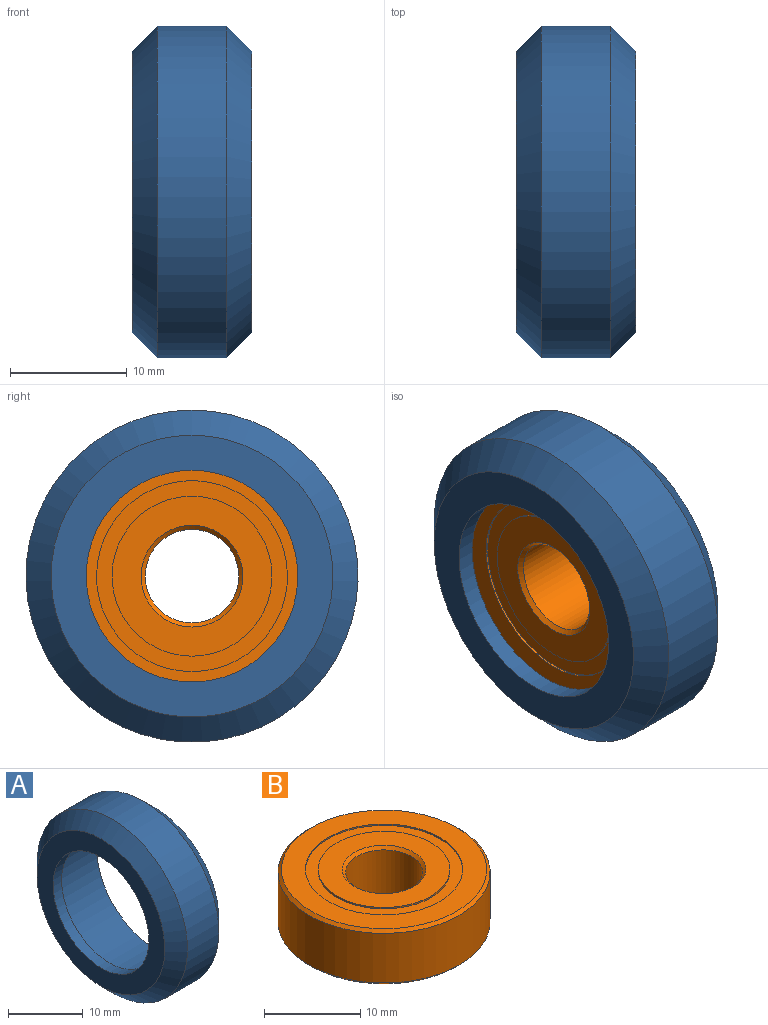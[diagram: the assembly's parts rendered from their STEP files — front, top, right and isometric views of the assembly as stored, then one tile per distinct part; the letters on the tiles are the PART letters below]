
ASSEMBLY  parts=2 mates=1
PART A: 8 faces, bbox 10.2x28.4x28.4 mm
  f0: cone r=14.2mm half-angle=45deg, axis (1,0,0), area 250.7mm2, adj f1,f7
  f1: plane 24.1x24.1mm, normal (-1,0,0), area 198.9mm2, adj f0,f2
  f2: cylinder r=9.05mm len=18.1mm, axis (-1,0,0), area 91mm2, adj f1,f3
  f3: plane 22.1x22.1mm, normal (1,0,0), area 126.3mm2, adj f2,f4
  f4: cylinder r=11.05mm len=22.1mm, axis (-1,0,0), area 597.1mm2, adj f3,f5
  f5: plane 24.1x24.1mm, normal (1,0,0), area 72.6mm2, adj f4,f6
  f6: cone r=12.05mm half-angle=45deg, axis (-1,0,0), area 250.7mm2, adj f5,f7
  f7: cylinder r=14.2mm len=28.4mm, axis (-1,0,0), area 526.4mm2, adj f0,f6
PART B: 156 faces, bbox 22x22x7 mm
  f0: cylinder r=8.16mm len=16.32mm, axis (0,0,1), area 9mm2, adj f6,f15
  f1: cylinder r=6.84mm len=13.68mm, axis (0,0,1), area 7.5mm2, adj f13,f15
  f2: cylinder r=8.16mm len=16.32mm, axis (0,0,1), area 9mm2, adj f7,f14
  f3: cone r=10.65mm half-angle=45deg, axis (0,0,1), area 33.7mm2, adj f4,f6
  f4: cylinder r=11mm len=22mm, axis (0,0,1), area 435.4mm2, adj f3,f5
  f5: cone r=11mm half-angle=45deg, axis (0,0,-1), area 33.7mm2, adj f4,f7
  f6: plane 21.3x21.3mm, normal (0,0,-1), area 147.2mm2, adj f0,f3
  f7: plane 21.3x21.3mm, normal (0,0,1), area 147.2mm2, adj f2,f5
  f8: cone r=4.35mm half-angle=45deg, axis (0,0,1), area 13mm2, adj f9,f12
  f9: cylinder r=4mm len=8mm, axis (0,0,1), area 158.3mm2, adj f8,f10
  f10: cone r=4mm half-angle=45deg, axis (0,0,-1), area 13mm2, adj f9,f13
  f11: cylinder r=6.84mm len=13.68mm, axis (0,0,1), area 7.5mm2, adj f12,f14
  f12: plane 13.68x13.68mm, normal (0,0,1), area 87.6mm2, adj f8,f11
  f13: plane 13.68x13.68mm, normal (0,0,-1), area 87.6mm2, adj f1,f10
  f14: plane 16.32x16.32mm, normal (0,0,1), area 62.1mm2, adj f2,f11
  f15: plane 16.32x16.32mm, normal (0,0,-1), area 62.1mm2, adj f0,f1
  f16: plane 1.59x1.53mm, normal (0,0,1), area 0.9mm2, adj f22,f23,f24,f25
  f17: torus R=7.5mm, axis (0,0,1), area 3.6mm2, adj f18,f22,f23,f25
  f18: cylinder r=8.16mm len=0.86mm, axis (0,0,1), area 0.1mm2, adj f17,f19,f22,f23
  f19: plane 1.59x1.53mm, normal (0,0,-1), area 0.9mm2, adj f18,f20,f22,f23
  f20: cylinder r=6.84mm len=0.57mm, axis (0,0,1), area 0.1mm2, adj f19,f21,f22,f23
  f21: torus R=7.5mm, axis (0,0,1), area 0.9mm2, adj f20,f22,f23,f24
  f22: sphere r=2.19mm, area 4.1mm2, adj f16,f17,f18,f19,f20,f21,f23,f24
  f23: sphere r=2.19mm, area 4.1mm2, adj f16,f17,f18,f19,f20,f21,f22,f24
  f24: cylinder r=6.84mm len=0.57mm, axis (0,0,1), area 0.1mm2, adj f16,f21,f22,f23
  f25: cylinder r=8.16mm len=0.86mm, axis (0,0,1), area 0.1mm2, adj f16,f17,f22,f23
  f26: plane 1.58x1.39mm, normal (0,0,1), area 0.9mm2, adj f32,f33,f34,f35
  f27: torus R=7.5mm, axis (0,0,1), area 1mm2, adj f28,f32,f33,f34
  f28: cylinder r=6.84mm len=0.65mm, axis (0,0,1), area 0.1mm2, adj f27,f29,f32,f33
  f29: plane 1.58x1.39mm, normal (0,0,-1), area 0.9mm2, adj f28,f30,f32,f33
  f30: cylinder r=8.16mm len=0.99mm, axis (0,0,1), area 0.1mm2, adj f29,f31,f32,f33
  f31: torus R=7.5mm, axis (0,0,1), area 3.7mm2, adj f30,f32,f33,f35
  f32: sphere r=2.19mm, area 4mm2, adj f26,f27,f28,f29,f30,f31,f33,f34
  f33: sphere r=2.19mm, area 4.1mm2, adj f26,f27,f28,f29,f30,f31,f32,f34
  f34: cylinder r=6.84mm len=0.65mm, axis (0,0,1), area 0.1mm2, adj f26,f27,f32,f33
  f35: cylinder r=8.16mm len=0.99mm, axis (0,0,1), area 0.1mm2, adj f26,f31,f32,f33
  f36: plane 1.33x1.1mm, normal (0,0,1), area 0.9mm2, adj f42,f43,f44,f45
  f37: torus R=7.5mm, axis (0,0,1), area 1mm2, adj f38,f42,f43,f44
  f38: cylinder r=6.84mm len=0.72mm, axis (0,0,1), area 0.1mm2, adj f37,f39,f42,f43
  f39: plane 1.33x1.1mm, normal (0,0,-1), area 0.9mm2, adj f38,f40,f42,f43
  f40: cylinder r=8.16mm len=1.1mm, axis (0,0,1), area 0.1mm2, adj f39,f41,f42,f43
  f41: torus R=7.5mm, axis (0,0,1), area 3.7mm2, adj f40,f42,f43,f45
  f42: sphere r=2.19mm, area 4mm2, adj f36,f37,f38,f39,f40,f41,f43,f44
  f43: sphere r=2.19mm, area 4.1mm2, adj f36,f37,f38,f39,f40,f41,f42,f44
  f44: cylinder r=6.84mm len=0.72mm, axis (0,0,1), area 0.1mm2, adj f36,f37,f42,f43
  f45: cylinder r=8.16mm len=1.1mm, axis (0,0,1), area 0.1mm2, adj f36,f41,f42,f43
  f46: plane 1.58x1.39mm, normal (0,0,1), area 0.9mm2, adj f52,f53,f54,f55
  f47: torus R=7.5mm, axis (0,0,1), area 1mm2, adj f48,f52,f53,f54
  f48: cylinder r=6.84mm len=0.65mm, axis (0,0,1), area 0.1mm2, adj f47,f49,f52,f53
  f49: plane 1.58x1.39mm, normal (0,0,-1), area 0.9mm2, adj f48,f50,f52,f53
  f50: cylinder r=8.16mm len=0.99mm, axis (0,0,1), area 0.1mm2, adj f49,f51,f52,f53
  f51: torus R=7.5mm, axis (0,0,1), area 3.7mm2, adj f50,f52,f53,f55
  f52: sphere r=2.19mm, area 4mm2, adj f46,f47,f48,f49,f50,f51,f53,f54
  f53: sphere r=2.19mm, area 4.1mm2, adj f46,f47,f48,f49,f50,f51,f52,f54
  f54: cylinder r=6.84mm len=0.65mm, axis (0,0,1), area 0.1mm2, adj f46,f47,f52,f53
  f55: cylinder r=8.16mm len=0.99mm, axis (0,0,1), area 0.1mm2, adj f46,f51,f52,f53
  f56: plane 1.59x1.53mm, normal (0,0,1), area 0.9mm2, adj f62,f63,f64,f65
  f57: torus R=7.5mm, axis (0,0,1), area 1mm2, adj f58,f62,f63,f64
  f58: cylinder r=6.84mm len=0.57mm, axis (0,0,1), area 0.1mm2, adj f57,f59,f62,f63
  f59: plane 1.59x1.53mm, normal (0,0,-1), area 0.9mm2, adj f58,f60,f62,f63
  f60: cylinder r=8.16mm len=0.86mm, axis (0,0,1), area 0.1mm2, adj f59,f61,f62,f63
  f61: torus R=7.5mm, axis (0,0,1), area 3.7mm2, adj f60,f62,f63,f65
  f62: sphere r=2.19mm, area 4mm2, adj f56,f57,f58,f59,f60,f61,f63,f64
  f63: sphere r=2.19mm, area 4.1mm2, adj f56,f57,f58,f59,f60,f61,f62,f64
  f64: cylinder r=6.84mm len=0.57mm, axis (0,0,1), area 0.1mm2, adj f56,f57,f62,f63
  f65: cylinder r=8.16mm len=0.86mm, axis (0,0,1), area 0.1mm2, adj f56,f61,f62,f63
  f66: plane 1.48x1.18mm, normal (0,0,1), area 0.9mm2, adj f72,f73,f74,f75
  f67: torus R=7.5mm, axis (0,0,1), area 1mm2, adj f68,f72,f73,f74
  f68: cylinder r=6.84mm len=0.71mm, axis (0,0,1), area 0.1mm2, adj f67,f69,f72,f73
  f69: plane 1.48x1.18mm, normal (0,0,-1), area 0.9mm2, adj f68,f70,f72,f73
  f70: cylinder r=8.16mm len=1.07mm, axis (0,0,1), area 0.1mm2, adj f69,f71,f72,f73
  f71: torus R=7.5mm, axis (0,0,1), area 3.7mm2, adj f70,f72,f73,f75
  f72: sphere r=2.19mm, area 4mm2, adj f66,f67,f68,f69,f70,f71,f73,f74
  f73: sphere r=2.19mm, area 4.1mm2, adj f66,f67,f68,f69,f70,f71,f72,f74
  f74: cylinder r=6.84mm len=0.71mm, axis (0,0,1), area 0.1mm2, adj f66,f67,f72,f73
  f75: cylinder r=8.16mm len=1.07mm, axis (0,0,1), area 0.1mm2, adj f66,f71,f72,f73
  f76: plane 1.48x1.18mm, normal (0,0,1), area 0.9mm2, adj f82,f83,f84,f85
  f77: torus R=7.5mm, axis (0,0,1), area 1mm2, adj f78,f82,f83,f84
  f78: cylinder r=6.84mm len=0.71mm, axis (0,0,1), area 0.1mm2, adj f77,f79,f82,f83
  f79: plane 1.48x1.18mm, normal (0,0,-1), area 0.9mm2, adj f78,f80,f82,f83
  f80: cylinder r=8.16mm len=1.07mm, axis (0,0,1), area 0.1mm2, adj f79,f81,f82,f83
  f81: torus R=7.5mm, axis (0,0,1), area 3.7mm2, adj f80,f82,f83,f85
  f82: sphere r=2.19mm, area 4mm2, adj f76,f77,f78,f79,f80,f81,f83,f84
  f83: sphere r=2.19mm, area 4.1mm2, adj f76,f77,f78,f79,f80,f81,f82,f84
  f84: cylinder r=6.84mm len=0.71mm, axis (0,0,1), area 0.1mm2, adj f76,f77,f82,f83
  f85: cylinder r=8.16mm len=1.07mm, axis (0,0,1), area 0.1mm2, adj f76,f81,f82,f83
  f86: plane 1.59x1.53mm, normal (0,0,1), area 0.9mm2, adj f92,f93,f94,f95
  f87: torus R=7.5mm, axis (0,0,1), area 1mm2, adj f88,f92,f93,f94
  f88: cylinder r=6.84mm len=0.57mm, axis (0,0,1), area 0.1mm2, adj f87,f89,f92,f93
  f89: plane 1.59x1.53mm, normal (0,0,-1), area 0.9mm2, adj f88,f90,f92,f93
  f90: cylinder r=8.16mm len=0.86mm, axis (0,0,1), area 0.1mm2, adj f89,f91,f92,f93
  f91: torus R=7.5mm, axis (0,0,1), area 3.7mm2, adj f90,f92,f93,f95
  f92: sphere r=2.19mm, area 4mm2, adj f86,f87,f88,f89,f90,f91,f93,f94
  f93: sphere r=2.19mm, area 4.1mm2, adj f86,f87,f88,f89,f90,f91,f92,f94
  f94: cylinder r=6.84mm len=0.57mm, axis (0,0,1), area 0.1mm2, adj f86,f87,f92,f93
  f95: cylinder r=8.16mm len=0.86mm, axis (0,0,1), area 0.1mm2, adj f86,f91,f92,f93
  f96: plane 1.58x1.39mm, normal (0,0,1), area 0.9mm2, adj f102,f103,f104,f105
  f97: torus R=7.5mm, axis (0,0,1), area 1mm2, adj f98,f102,f103,f104
  f98: cylinder r=6.84mm len=0.65mm, axis (0,0,1), area 0.1mm2, adj f97,f99,f102,f103
  f99: plane 1.58x1.39mm, normal (0,0,-1), area 0.9mm2, adj f98,f100,f102,f103
  f100: cylinder r=8.16mm len=0.99mm, axis (0,0,1), area 0.1mm2, adj f99,f101,f102,f103
  f101: torus R=7.5mm, axis (0,0,1), area 3.7mm2, adj f100,f102,f103,f105
  f102: sphere r=2.19mm, area 4mm2, adj f96,f97,f98,f99,f100,f101,f103,f104
  f103: sphere r=2.19mm, area 4.1mm2, adj f96,f97,f98,f99,f100,f101,f102,f104
  f104: cylinder r=6.84mm len=0.65mm, axis (0,0,1), area 0.1mm2, adj f96,f97,f102,f103
  f105: cylinder r=8.16mm len=0.99mm, axis (0,0,1), area 0.1mm2, adj f96,f101,f102,f103
  f106: plane 1.33x1.1mm, normal (0,0,1), area 0.9mm2, adj f112,f113,f114,f115
  f107: torus R=7.5mm, axis (0,0,1), area 1mm2, adj f108,f112,f113,f114
  f108: cylinder r=6.84mm len=0.72mm, axis (0,0,1), area 0.1mm2, adj f107,f109,f112,f113
  f109: plane 1.33x1.1mm, normal (0,0,-1), area 0.9mm2, adj f108,f110,f112,f113
  f110: cylinder r=8.16mm len=1.1mm, axis (0,0,1), area 0.1mm2, adj f109,f111,f112,f113
  f111: torus R=7.5mm, axis (0,0,1), area 3.7mm2, adj f110,f112,f113,f115
  f112: sphere r=2.19mm, area 4mm2, adj f106,f107,f108,f109,f110,f111,f113,f114
  f113: sphere r=2.19mm, area 4.1mm2, adj f106,f107,f108,f109,f110,f111,f112,f114
  f114: cylinder r=6.84mm len=0.72mm, axis (0,0,1), area 0.1mm2, adj f106,f107,f112,f113
  f115: cylinder r=8.16mm len=1.1mm, axis (0,0,1), area 0.1mm2, adj f106,f111,f112,f113
  f116: plane 1.58x1.39mm, normal (0,0,1), area 0.9mm2, adj f122,f123,f124,f125
  f117: torus R=7.5mm, axis (0,0,1), area 1mm2, adj f118,f122,f123,f124
  f118: cylinder r=6.84mm len=0.65mm, axis (0,0,1), area 0.1mm2, adj f117,f119,f122,f123
  f119: plane 1.58x1.39mm, normal (0,0,-1), area 0.9mm2, adj f118,f120,f122,f123
  f120: cylinder r=8.16mm len=0.99mm, axis (0,0,1), area 0.1mm2, adj f119,f121,f122,f123
  f121: torus R=7.5mm, axis (0,0,1), area 3.7mm2, adj f120,f122,f123,f125
  f122: sphere r=2.19mm, area 4mm2, adj f116,f117,f118,f119,f120,f121,f123,f124
  f123: sphere r=2.19mm, area 4.1mm2, adj f116,f117,f118,f119,f120,f121,f122,f124
  f124: cylinder r=6.84mm len=0.65mm, axis (0,0,1), area 0.1mm2, adj f116,f117,f122,f123
  f125: cylinder r=8.16mm len=0.99mm, axis (0,0,1), area 0.1mm2, adj f116,f121,f122,f123
  f126: plane 1.59x1.53mm, normal (0,0,1), area 0.9mm2, adj f132,f133,f134,f135
  f127: torus R=7.5mm, axis (0,0,1), area 1mm2, adj f128,f132,f133,f134
  f128: cylinder r=6.84mm len=0.57mm, axis (0,0,1), area 0.1mm2, adj f127,f129,f132,f133
  f129: plane 1.59x1.53mm, normal (0,0,-1), area 0.9mm2, adj f128,f130,f132,f133
  f130: cylinder r=8.16mm len=0.86mm, axis (0,0,1), area 0.1mm2, adj f129,f131,f132,f133
  f131: torus R=7.5mm, axis (0,0,1), area 3.7mm2, adj f130,f132,f133,f135
  f132: sphere r=2.19mm, area 4mm2, adj f126,f127,f128,f129,f130,f131,f133,f134
  f133: sphere r=2.19mm, area 4.1mm2, adj f126,f127,f128,f129,f130,f131,f132,f134
  f134: cylinder r=6.84mm len=0.57mm, axis (0,0,1), area 0.1mm2, adj f126,f127,f132,f133
  f135: cylinder r=8.16mm len=0.86mm, axis (0,0,1), area 0.1mm2, adj f126,f131,f132,f133
  f136: plane 1.48x1.18mm, normal (0,0,1), area 0.9mm2, adj f142,f143,f144,f145
  f137: torus R=7.5mm, axis (0,0,1), area 1mm2, adj f138,f142,f143,f144
  f138: cylinder r=6.84mm len=0.71mm, axis (0,0,1), area 0.1mm2, adj f137,f139,f142,f143
  f139: plane 1.48x1.18mm, normal (0,0,-1), area 0.9mm2, adj f138,f140,f142,f143
  f140: cylinder r=8.16mm len=1.07mm, axis (0,0,1), area 0.1mm2, adj f139,f141,f142,f143
  f141: torus R=7.5mm, axis (0,0,1), area 3.7mm2, adj f140,f142,f143,f145
  f142: sphere r=2.19mm, area 4mm2, adj f136,f137,f138,f139,f140,f141,f143,f144
  f143: sphere r=2.19mm, area 4.1mm2, adj f136,f137,f138,f139,f140,f141,f142,f144
  f144: cylinder r=6.84mm len=0.71mm, axis (0,0,1), area 0.1mm2, adj f136,f137,f142,f143
  f145: cylinder r=8.16mm len=1.07mm, axis (0,0,1), area 0.1mm2, adj f136,f141,f142,f143
  f146: plane 1.48x1.18mm, normal (0,0,1), area 0.9mm2, adj f152,f153,f154,f155
  f147: torus R=7.5mm, axis (0,0,1), area 3.6mm2, adj f148,f152,f153,f155
  f148: cylinder r=8.16mm len=1.07mm, axis (0,0,1), area 0.1mm2, adj f147,f149,f152,f153
  f149: plane 1.48x1.18mm, normal (0,0,-1), area 0.9mm2, adj f148,f150,f152,f153
  f150: cylinder r=6.84mm len=0.71mm, axis (0,0,1), area 0.1mm2, adj f149,f151,f152,f153
  f151: torus R=7.5mm, axis (0,0,1), area 0.9mm2, adj f150,f152,f153,f154
  f152: sphere r=2.19mm, area 4.1mm2, adj f146,f147,f148,f149,f150,f151,f153,f154
  f153: sphere r=2.19mm, area 4.1mm2, adj f146,f147,f148,f149,f150,f151,f152,f154
  f154: cylinder r=6.84mm len=0.71mm, axis (0,0,1), area 0.1mm2, adj f146,f151,f152,f153
  f155: cylinder r=8.16mm len=1.07mm, axis (0,0,1), area 0.1mm2, adj f146,f147,f152,f153
PLACE A at identity fixed
PLACE B rot(axis=(0.71,0,-0.71),180deg) t=(0.8,0,0)mm
MATE fastened A.f0 <-> B.f0  axis (-1,0,0) through (0.8,0,0)mm
